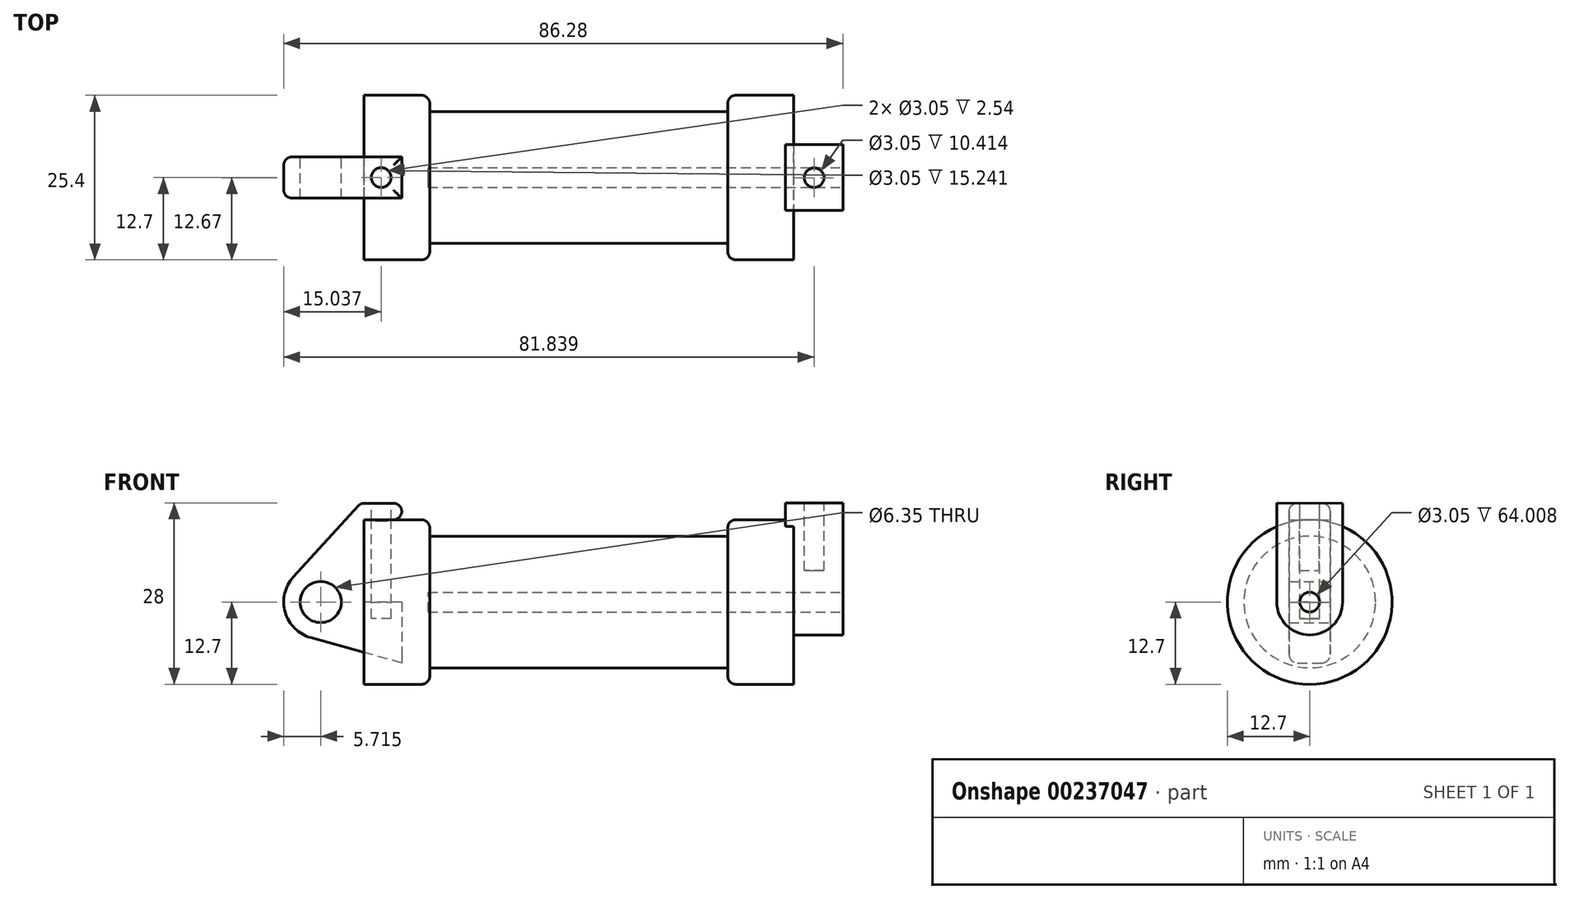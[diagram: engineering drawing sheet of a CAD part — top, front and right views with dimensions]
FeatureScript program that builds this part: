
annotation { "Feature Type Name" : "Feature", "Feature Type Description" : "" }
export const myFeature = defineFeature(function(context is Context, id is Id, definition is map)
    precondition{}
    {
        {
            var Q0;
            Q0=qCreatedBy(makeId("Front.planeOp"),FACE);
            var sketch = newSketch(context, id + "F0", { "sketchPlane" : qUnion([Q0])});
            skLineSegment(sketch, "E0", {"start": v(0, 0) * mm, "end": v(0, 12.7) * mm});
            skLineSegment(sketch, "E1", {"start": v(0, 12.7) * mm, "end": v(10.16, 12.7) * mm});
            skLineSegment(sketch, "E2", {"start": v(10.16, 12.7) * mm, "end": v(10.16, 10.16) * mm});
            skLineSegment(sketch, "E3", {"start": v(10.16, 10.16) * mm, "end": v(56.13, 10.16) * mm});
            skLineSegment(sketch, "E4", {"start": v(56.13, 10.16) * mm, "end": v(56.13, 12.7) * mm});
            skLineSegment(sketch, "E5", {"start": v(56.13, 12.7) * mm, "end": v(66.3, 12.7) * mm});
            skLineSegment(sketch, "E6", {"start": v(66.3, 12.7) * mm, "end": v(66.3, 0) * mm});
            skLineSegment(sketch, "E7", {"start": v(66.3, 0) * mm, "end": v(0, 0) * mm});
            skLineSegment(sketch, "E8", {"start": v(5.84, 15.24) * mm, "end": v(-0.5, 15.24) * mm});
            skLineSegment(sketch, "E9", {"start": v(-0.5, 15.24) * mm, "end": v(-10.88, 3.85) * mm});
            skLineSegment(sketch, "E10", {"start": v(0, 0) * mm, "end": v(-6.65, 0) * mm});
            skCircle(sketch, "E11", {"center": v(-6.65, 0) * mm, "radius": 5.72 * mm});
            skCircle(sketch, "E12", {"center": v(-6.65, 0) * mm, "radius": 3.18 * mm});
            skLineSegment(sketch, "E13", {"start": v(5.84, 15.24) * mm, "end": v(5.84, -9.4) * mm});
            skLineSegment(sketch, "E14", {"start": v(5.84, -9.4) * mm, "end": v(-8.18, -5.5) * mm});
            skSolve(sketch);
        }
        {
            var Q0;
            {var subQ0=sQuery(id+"F0.wireOp",EDGE,"E2");Q0=makeQuery(id+"F0.imprint","IMPRINT",FACE,{"disambiguationData":[TD([[makeQuery(id+"F0.imprint","IMPRINT",EDGE,{"derivedFrom":subQ0}),-1.0]])]});}
            var Q1;
            {var subQ0=sQuery(id+"F0.wireOp",EDGE,"E0");Q1=makeQuery(id+"F0.imprint","IMPRINT",FACE,{"disambiguationData":[TD([[makeQuery(id+"F0.imprint","IMPRINT",EDGE,{"derivedFrom":subQ0}),-1.0]])]});}
            var Q2;
            Q2=sQuery(id+"F0.wireOp",EDGE,"E7");
            revolve(context, id + "F1", {"entities" : qUnion([Q0, Q1]), "axis" : qUnion([Q2]), "revolveType" : RevolveType.FULL});
        }
        {
            var Q0;
            {var subQ3=sQuery(id+"F0.wireOp",EDGE,"E0");Q0=makeQuery(id+"F0.imprint","IMPRINT",FACE,{"disambiguationData":[TD([[makeQuery(id+"F0.imprint","IMPRINT",EDGE,{"derivedFrom":subQ3}),1.0]])]});}
            var Q1;
            {var subQ4=sQuery(id+"F0.wireOp",EDGE,"E12");Q1=makeQuery(id+"F0.imprint","IMPRINT",FACE,{"disambiguationData":[TD([[makeQuery(id+"F0.imprint","IMPRINT",EDGE,{"derivedFrom":subQ4}),-1.0]])]});}
            var Q2;
            {var subQ0=sQuery(id+"F0.wireOp",EDGE,"E14");Q2=makeQuery(id+"F0.imprint","IMPRINT",FACE,{"disambiguationData":[TD([[makeQuery(id+"F0.imprint","IMPRINT",EDGE,{"derivedFrom":subQ0}),-1.0]])]});}
            extrude(context, id + "F2", {"entities" : qUnion([Q0, Q1, Q2]), "endBound" : BoundingType.SYMMETRIC, "depth" : 6.35 * mm});
        }
        {
            var Q0;
            Q0=makeQuery(id+"F1.opRevolve","SWEPT_FACE",FACE,{"disambiguationData":[OSD([sQuery(id+"F0.wireOp",EDGE,"E6")])]});
            var sketch = newSketch(context, id + "F3", { "sketchPlane" : qUnion([Q0])});
            skCircle(sketch, "E15", {"center": v(0, 0) * mm, "radius": 1.52 * mm});
            skCircle(sketch, "E16", {"center": v(0, 0) * mm, "radius": 5.08 * mm});
            skLineSegment(sketch, "E17", {"start": v(-5.08, 0) * mm, "end": v(-5.08, 15.3) * mm});
            skLineSegment(sketch, "E18", {"start": v(5.08, 0) * mm, "end": v(5.08, 15.24) * mm});
            skLineSegment(sketch, "E19", {"start": v(5.08, 15.24) * mm, "end": v(-5.08, 15.3) * mm});
            skSolve(sketch);
        }
        {
            var Q0;
            Q0=makeQuery(id+"F3.imprint","IMPRINT",FACE,{"disambiguationData":[TD([[makeQuery(id+"F3.imprint","IMPRINT",EDGE,{"derivedFrom":sQuery(id+"F3.wireOp",EDGE,"E15")}),1.0]])]});
            extrude(context, id + "F4", {"entities" : qUnion([Q0]), "operationType" : NewBodyOperationType.REMOVE, "oppositeDirection" : true, "depth" : 56.4 * mm});
        }
        {
            var Q0;
            Q0 = qSketchRegion(id + "F3", true);
            extrude(context, id + "F5", {"entities" : qUnion([Q0]), "operationType" : NewBodyOperationType.ADD, "depth" : 7.62 * mm, "hasSecondDirection" : true, "secondDirectionOppositeDirection" : true, "secondDirectionDepth" : 1.27 * mm});
        }
        {
            var Q0;
            Q0=makeQuery(id+"F2.opExtrude","SWEPT_FACE",FACE,{"disambiguationData":[OSD([sQuery(id+"F0.wireOp",EDGE,"E8")])]});
            var sketch = newSketch(context, id + "F6", { "sketchPlane" : qUnion([Q0])});
            skCircle(sketch, "E20", {"center": v(2.67, 0) * mm, "radius": 1.52 * mm});
            skSolve(sketch);
        }
        {
            var Q0;
            Q0=makeQuery(id+"F5.opExtrude","SWEPT_FACE",FACE,{"disambiguationData":[OSD([sQuery(id+"F3.wireOp",EDGE,"E19")])]});
            var sketch = newSketch(context, id + "F7", { "sketchPlane" : qUnion([Q0])});
            skCircle(sketch, "E21", {"center": v(69.47, -0.09) * mm, "radius": 1.52 * mm});
            skSolve(sketch);
        }
        {
            var Q0;
            Q0=makeQuery(id+"F7.imprint","IMPRINT",FACE,{"disambiguationData":[TD([[makeQuery(id+"F7.imprint","IMPRINT",EDGE,{"derivedFrom":sQuery(id+"F7.wireOp",EDGE,"E21")}),1.0]])]});
            extrude(context, id + "F8", {"entities" : qUnion([Q0]), "operationType" : NewBodyOperationType.REMOVE, "oppositeDirection" : true, "depth" : 10.4 * mm});
        }
        {
            var Q0;
            Q0 = qSketchRegion(id + "F6", true);
            extrude(context, id + "F9", {"entities" : qUnion([Q0]), "operationType" : NewBodyOperationType.REMOVE, "oppositeDirection" : true, "depth" : 17.78 * mm});
        }
        {
            var Q0;
            Q0=makeQuery(id+"F1.opRevolve","SWEPT_EDGE",EDGE,{"disambiguationData":[OSD([sQuery(id+"F0.wireOp",EDGE,"E1"),sQuery(id+"F0.wireOp",EDGE,"E2")])]});
            fillet(context, id + "F10", {"entities" : qUnion([Q0]), "radius" : 1.27 * mm, "tangentPropagation" : true, "allowEdgeOverflow" : false});
        }
        {
            var Q0;
            Q0=makeQuery(id+"F1.opRevolve","SWEPT_EDGE",EDGE,{"disambiguationData":[OSD([sQuery(id+"F0.wireOp",EDGE,"E4"),sQuery(id+"F0.wireOp",EDGE,"E5")])]});
            fillet(context, id + "F11", {"entities" : qUnion([Q0]), "radius" : 1.27 * mm, "tangentPropagation" : true, "allowEdgeOverflow" : false});
        }
        {
            var Q0;
            Q0=makeQuery(id+"F2.opExtrude","CAP_EDGE",EDGE,{"disambiguationData":[OSD([sQuery(id+"F0.wireOp",EDGE,"E8")])],"isStart":true});
            var Q1;
            Q1=makeQuery(id+"F2.opExtrude","SWEPT_EDGE",EDGE,{"disambiguationData":[OSD([sQuery(id+"F0.wireOp",EDGE,"E8"),sQuery(id+"F0.wireOp",EDGE,"E13")])]});
            var Q2;
            Q2=makeQuery(id+"F2.opExtrude","CAP_EDGE",EDGE,{"disambiguationData":[OSD([sQuery(id+"F0.wireOp",EDGE,"E8")])],"isStart":false});
            var Q3;
            Q3=makeQuery(id+"F2.opExtrude","SWEPT_FACE",FACE,{"disambiguationData":[OSD([sQuery(id+"F0.wireOp",EDGE,"E9")])]});
            var Q4;
            Q4=makeQuery(id+"F1.opRevolve","SWEPT_EDGE",EDGE,{"disambiguationData":[OSD([sQuery(id+"F0.wireOp",EDGE,"E5"),sQuery(id+"F0.wireOp",EDGE,"E6")])]});
            var Q5;
            Q5=makeQuery(id+"F5.opExtrude","CAP_EDGE",EDGE,{"disambiguationData":[OSD([sQuery(id+"F3.wireOp",EDGE,"E18")])],"isStart":false});
            var Q6;
            Q6=makeQuery(id+"F5.opExtrude","CAP_EDGE",EDGE,{"disambiguationData":[OSD([sQuery(id+"F3.wireOp",EDGE,"E16")])],"isStart":false});
            var Q7;
            Q7=makeQuery(id+"F1.opRevolve","SWEPT_FACE",FACE,{"disambiguationData":[OSD([sQuery(id+"F0.wireOp",EDGE,"E6")])]});
            var Q8;
            Q8=makeQuery(id+"F5.opExtrude","SWEPT_EDGE",EDGE,{"disambiguationData":[OSD([sQuery(id+"F3.wireOp",EDGE,"E17"),sQuery(id+"F3.wireOp",EDGE,"E19")])]});
            var Q9;
            Q9=makeQuery(id+"F5.opExtrude","CAP_EDGE",EDGE,{"disambiguationData":[OSD([sQuery(id+"F3.wireOp",EDGE,"E19")])],"isStart":false});
            var Q10;
            Q10=makeQuery(id+"F5.opExtrude","SWEPT_EDGE",EDGE,{"disambiguationData":[OSD([sQuery(id+"F3.wireOp",EDGE,"E18"),sQuery(id+"F3.wireOp",EDGE,"E19")])]});
            var Q11;
            Q11=makeQuery(id+"F5.opExtrude","CAP_EDGE",EDGE,{"disambiguationData":[OSD([sQuery(id+"F3.wireOp",EDGE,"E19")])],"isStart":true});
            var Q12;
            Q12=makeQuery(id+"F1.opRevolve","SWEPT_FACE",FACE,{"disambiguationData":[OSD([sQuery(id+"F0.wireOp",EDGE,"E0")])]});
            var Q13;
            Q13=makeQuery(id+"F2.opExtrude","SWEPT_EDGE",EDGE,{"disambiguationData":[OSD([sQuery(id+"F0.wireOp",EDGE,"E1"),sQuery(id+"F0.wireOp",EDGE,"E13")])]});
            fillet(context, id + "F12", {"entities" : qUnion([Q0, Q1, Q2, Q3, Q4, Q5, Q6, Q7, Q8, Q9, Q10, Q11, Q12, Q13]), "radius" : 1.27 * mm, "tangentPropagation" : true, "allowEdgeOverflow" : false});
        }
    });
